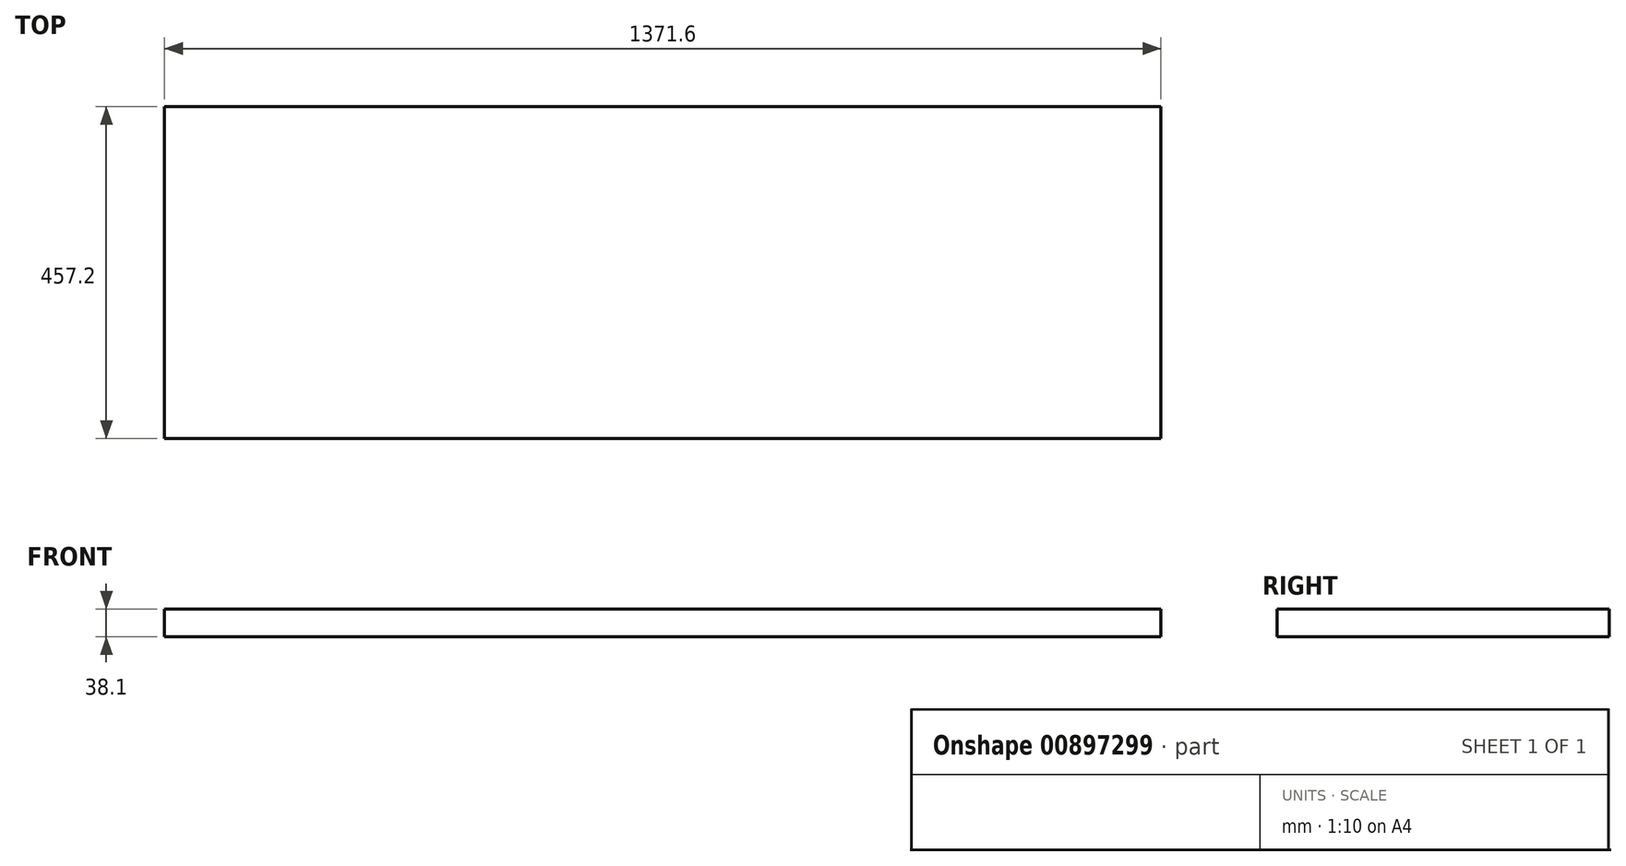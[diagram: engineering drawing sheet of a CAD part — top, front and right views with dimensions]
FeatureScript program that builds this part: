
annotation { "Feature Type Name" : "Feature", "Feature Type Description" : "" }
export const myFeature = defineFeature(function(context is Context, id is Id, definition is map)
    precondition{}
    {
        {
            var Q0;
            Q0=qCreatedBy(makeId("Top.planeOp"),FACE);
            var sketch = newSketch(context, id + "F0", { "sketchPlane" : qUnion([Q0])});
            skLineSegment(sketch, "E0.bottom", {"start": v(-1312.84, 408.17) * mm, "end": v(58.76, 408.17) * mm});
            skLineSegment(sketch, "E0.top", {"start": v(-1312.84, -49.03) * mm, "end": v(58.76, -49.03) * mm});
            skLineSegment(sketch, "E0.left", {"start": v(-1312.84, 408.17) * mm, "end": v(-1312.84, -49.03) * mm});
            skLineSegment(sketch, "E0.right", {"start": v(58.76, 408.17) * mm, "end": v(58.76, -49.03) * mm});
            skSolve(sketch);
        }
        {
            var Q0;
            Q0=makeQuery(id+"F0.imprint","IMPRINT",FACE,{"disambiguationData":[TD([[makeQuery(id+"F0.imprint","IMPRINT",EDGE,{"derivedFrom":sQuery(id+"F0.wireOp",EDGE,"E0.bottom")}),-1.0]])]});
            extrude(context, id + "F1", {"entities" : qUnion([Q0]), "depth" : 38.1 * mm, "offsetDistance" : 25.4 * mm});
        }
    });
